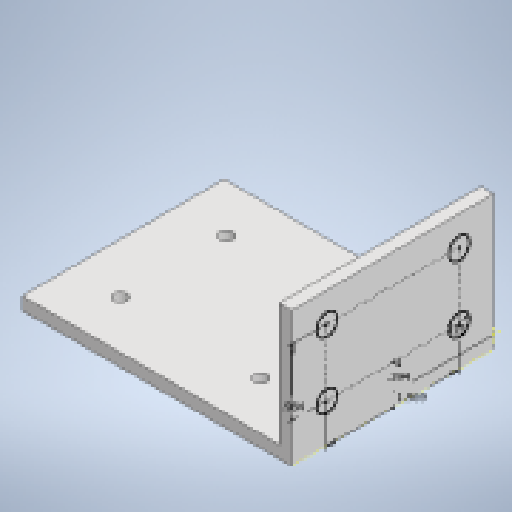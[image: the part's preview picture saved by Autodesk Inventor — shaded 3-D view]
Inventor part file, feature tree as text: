
AUTODESK INVENTOR PART (.ipt)
format: ipt  version: 2023 (Build 270158000, 158)  size: 160,256 bytes
history: native  units: in
note: dims shown in document units (in); Inventor stores cm internally (conversion verified against a paired STEP export)
features: extrude x3, sketch x3
ambient origin geometry x8: Origin, YZ Plane, XZ Plane, XY Plane, X Axis, Y Axis, Z Axis, Center Point
bodies: Solid1 (feature_tree)
feature tree (6):
  extrude  "Extrusion1"  Depth=2.0in
  extrude  "Extrusion2"  Depth=3.0in TaperAngle=0.0deg
  extrude  "Extrusion3"  Depth=0.3937in
  sketch  "Sketch1"  dims[d0=4.0in d1=2.0in]
  sketch  "Sketch2"  dims[d2=0.1875in d3=3.0in d4=0.0in]
  sketch  "Sketch3"  dims[d5=2.0866in d6=1.5748in d7=2.2126in d8=0.1969in d9=3.0in d10=0.0in d11=1.811in d12=0.9843in d13=0.3937in d14=0.315in d15=1.0in d16=0.0in]
